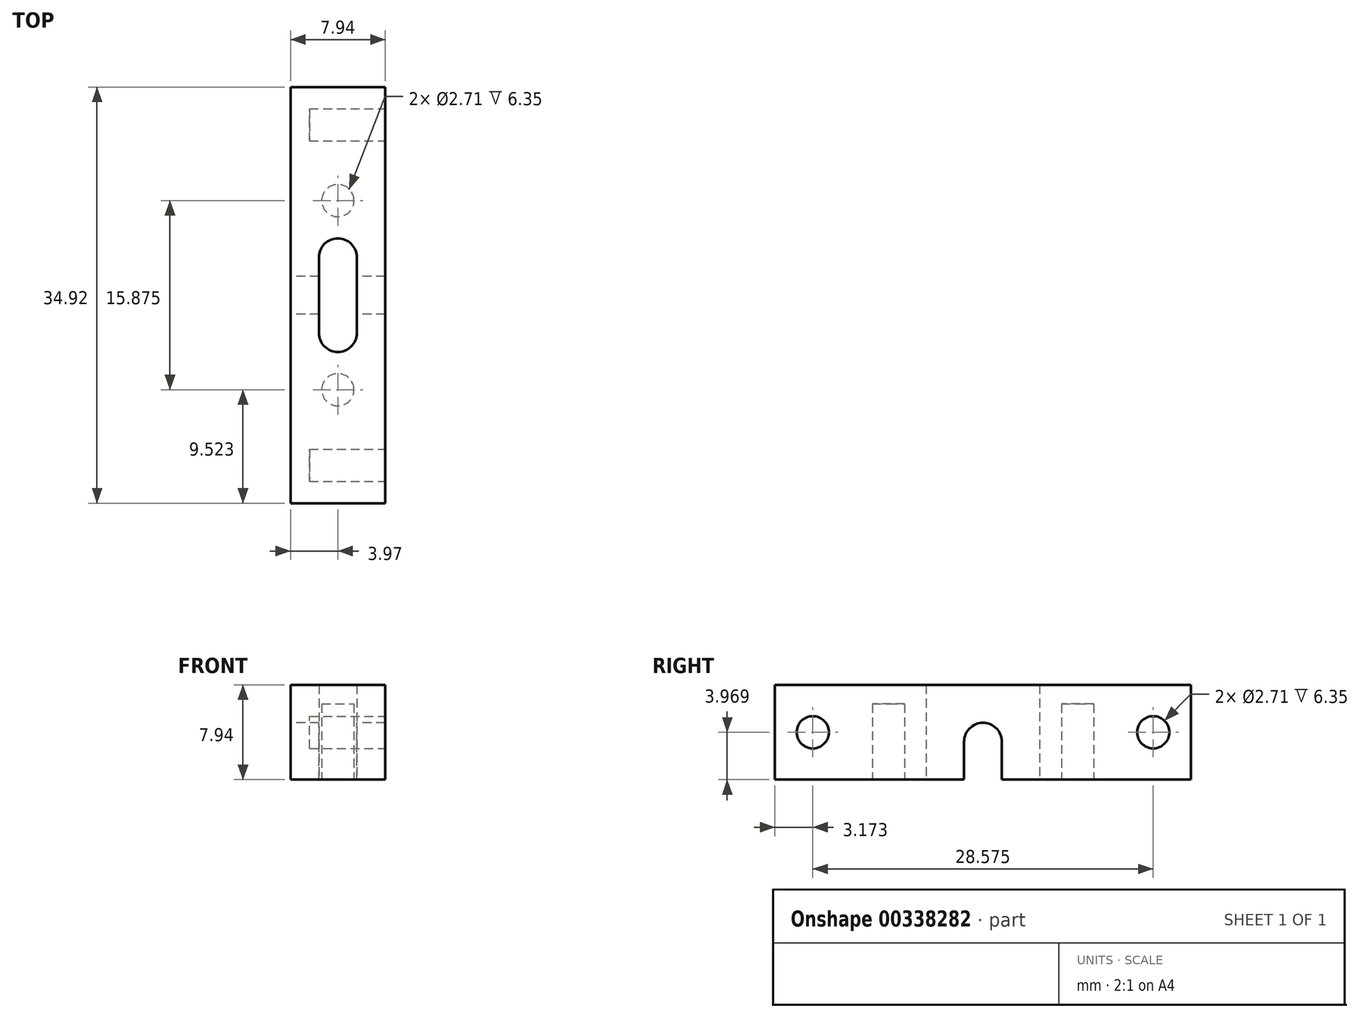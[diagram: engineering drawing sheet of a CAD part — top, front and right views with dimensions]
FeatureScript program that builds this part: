
annotation { "Feature Type Name" : "Feature", "Feature Type Description" : "" }
export const myFeature = defineFeature(function(context is Context, id is Id, definition is map)
    precondition{}
    {
        {
            var Q0;
            Q0=qCreatedBy(makeId("Top.planeOp"),FACE);
            var sketch = newSketch(context, id + "F0", { "sketchPlane" : qUnion([Q0])});
            skLineSegment(sketch, "E0.bottom", {"start": v(3.97, -17.46) * mm, "end": v(-3.97, -17.46) * mm});
            skLineSegment(sketch, "E0.top", {"start": v(3.97, 17.46) * mm, "end": v(-3.97, 17.46) * mm});
            skLineSegment(sketch, "E0.left", {"start": v(3.97, -17.46) * mm, "end": v(3.97, 17.46) * mm});
            skLineSegment(sketch, "E0.right", {"start": v(-3.97, -17.46) * mm, "end": v(-3.97, 17.46) * mm});
            skPoint(sketch, "E0.middle", {"position": v(0, 0) * mm});
            skLineSegment(sketch, "E1.bottom", {"start": v(1.59, -3.18) * mm, "end": v(-1.59, -3.18) * mm, "construction": true});
            skLineSegment(sketch, "E1.top", {"start": v(1.59, 3.18) * mm, "end": v(-1.59, 3.18) * mm, "construction": true});
            skLineSegment(sketch, "E1.left", {"start": v(1.59, -3.18) * mm, "end": v(1.59, 3.18) * mm});
            skLineSegment(sketch, "E1.right", {"start": v(-1.59, -3.18) * mm, "end": v(-1.59, 3.18) * mm});
            skArc(sketch, "E2", {"start": v(-1.59, -3.18) * mm, "mid": v(0, -4.76) * mm, "end": v(1.59, -3.18) * mm});
            skArc(sketch, "E3", {"start": v(1.59, 3.18) * mm, "mid": v(0, 4.76) * mm, "end": v(-1.59, 3.18) * mm});
            skLineSegment(sketch, "E4", {"start": v(0, 3.18) * mm, "end": v(0, 4.76) * mm, "construction": true});
            skLineSegment(sketch, "E5", {"start": v(0, 4.76) * mm, "end": v(0, 17.46) * mm, "construction": true});
            skSolve(sketch);
        }
        {
            var Q0;
            Q0 = qSketchRegion(id + "F0", true);
            extrude(context, id + "F1", {"entities" : qUnion([Q0]), "depth" : 7.94 * mm});
        }
        {
            var Q0;
            Q0=makeQuery(id+"F1.opExtrude","CAP_FACE",FACE,{"disambiguationData":[OSD([sQuery(id+"F0.wireOp",EDGE,"E0.bottom"),sQuery(id+"F0.wireOp",EDGE,"E0.top"),sQuery(id+"F0.wireOp",EDGE,"E0.left"),sQuery(id+"F0.wireOp",EDGE,"E0.right"),sQuery(id+"F0.wireOp",EDGE,"E1.left"),sQuery(id+"F0.wireOp",EDGE,"E1.right"),sQuery(id+"F0.wireOp",EDGE,"E2"),sQuery(id+"F0.wireOp",EDGE,"E3")])],"isStart":true});
            var sketch = newSketch(context, id + "F2", { "sketchPlane" : qUnion([Q0])});
            skLineSegment(sketch, "E6", {"start": v(0, -4.76) * mm, "end": v(0, -7.94) * mm, "construction": true});
            skLineSegment(sketch, "E7", {"start": v(0, 4.76) * mm, "end": v(0, 7.94) * mm, "construction": true});
            skCircle(sketch, "E8", {"center": v(0, -7.94) * mm, "radius": 1.35 * mm});
            skCircle(sketch, "E9", {"center": v(0, 7.94) * mm, "radius": 1.35 * mm});
            skSolve(sketch);
        }
        {
            var Q0;
            Q0 = qSketchRegion(id + "F2", true);
            extrude(context, id + "F3", {"entities" : qUnion([Q0]), "operationType" : NewBodyOperationType.REMOVE, "oppositeDirection" : true, "depth" : 6.35 * mm});
        }
        {
            var Q0;
            Q0=makeQuery(id+"F1.opExtrude","SWEPT_FACE",FACE,{"disambiguationData":[OSD([sQuery(id+"F0.wireOp",EDGE,"E0.left")])]});
            var sketch = newSketch(context, id + "F4", { "sketchPlane" : qUnion([Q0])});
            skLineSegment(sketch, "E10.bottom", {"start": v(17.46, 3.97) * mm, "end": v(14.29, 3.97) * mm, "construction": true});
            skLineSegment(sketch, "E10.top", {"start": v(17.46, 7.94) * mm, "end": v(14.29, 7.94) * mm, "construction": true});
            skLineSegment(sketch, "E10.left", {"start": v(17.46, 3.97) * mm, "end": v(17.46, 7.94) * mm, "construction": true});
            skLineSegment(sketch, "E10.right", {"start": v(14.29, 3.97) * mm, "end": v(14.29, 7.94) * mm, "construction": true});
            skLineSegment(sketch, "E11.bottom", {"start": v(-17.46, 3.97) * mm, "end": v(-14.29, 3.97) * mm, "construction": true});
            skLineSegment(sketch, "E11.top", {"start": v(-17.46, 7.94) * mm, "end": v(-14.29, 7.94) * mm, "construction": true});
            skLineSegment(sketch, "E11.left", {"start": v(-17.46, 3.97) * mm, "end": v(-17.46, 7.94) * mm, "construction": true});
            skLineSegment(sketch, "E11.right", {"start": v(-14.29, 3.97) * mm, "end": v(-14.29, 7.94) * mm, "construction": true});
            skCircle(sketch, "E12", {"center": v(14.29, 3.97) * mm, "radius": 1.35 * mm});
            skCircle(sketch, "E13", {"center": v(-14.29, 3.97) * mm, "radius": 1.35 * mm});
            skSolve(sketch);
        }
        {
            var Q0;
            Q0 = qSketchRegion(id + "F4", true);
            extrude(context, id + "F5", {"entities" : qUnion([Q0]), "operationType" : NewBodyOperationType.REMOVE, "oppositeDirection" : true, "depth" : 6.35 * mm});
        }
        {
            var Q0;
            Q0=makeQuery(id+"F1.opExtrude","SWEPT_FACE",FACE,{"disambiguationData":[OSD([sQuery(id+"F0.wireOp",EDGE,"E0.right")])]});
            var sketch = newSketch(context, id + "F6", { "sketchPlane" : qUnion([Q0])});
            skLineSegment(sketch, "E14.bottom", {"start": v(-1.59, 0) * mm, "end": v(1.59, 0) * mm});
            skLineSegment(sketch, "E14.top", {"start": v(-1.59, 3.17) * mm, "end": v(1.59, 3.17) * mm, "construction": true});
            skLineSegment(sketch, "E14.left", {"start": v(-1.59, 0) * mm, "end": v(-1.59, 3.17) * mm});
            skLineSegment(sketch, "E14.right", {"start": v(1.59, 0) * mm, "end": v(1.59, 3.17) * mm});
            skArc(sketch, "E15", {"start": v(1.59, 3.17) * mm, "mid": v(0, 4.76) * mm, "end": v(-1.59, 3.17) * mm});
            skLineSegment(sketch, "E16", {"start": v(0, 3.17) * mm, "end": v(0, 7.94) * mm, "construction": true});
            skSolve(sketch);
        }
        {
            var Q0;
            Q0 = qSketchRegion(id + "F6", true);
            var Q1;
            Q1=makeQuery(id+"F1.opExtrude","SWEPT_FACE",FACE,{"disambiguationData":[OSD([sQuery(id+"F0.wireOp",EDGE,"E0.left")])]});
            extrude(context, id + "F7", {"entities" : qUnion([Q0]), "operationType" : NewBodyOperationType.REMOVE, "endBound" : BoundingType.UP_TO_SURFACE, "oppositeDirection" : true, "endBoundEntityFace" : qUnion([Q1]), "depth" : 25.4 * mm});
        }
    });
